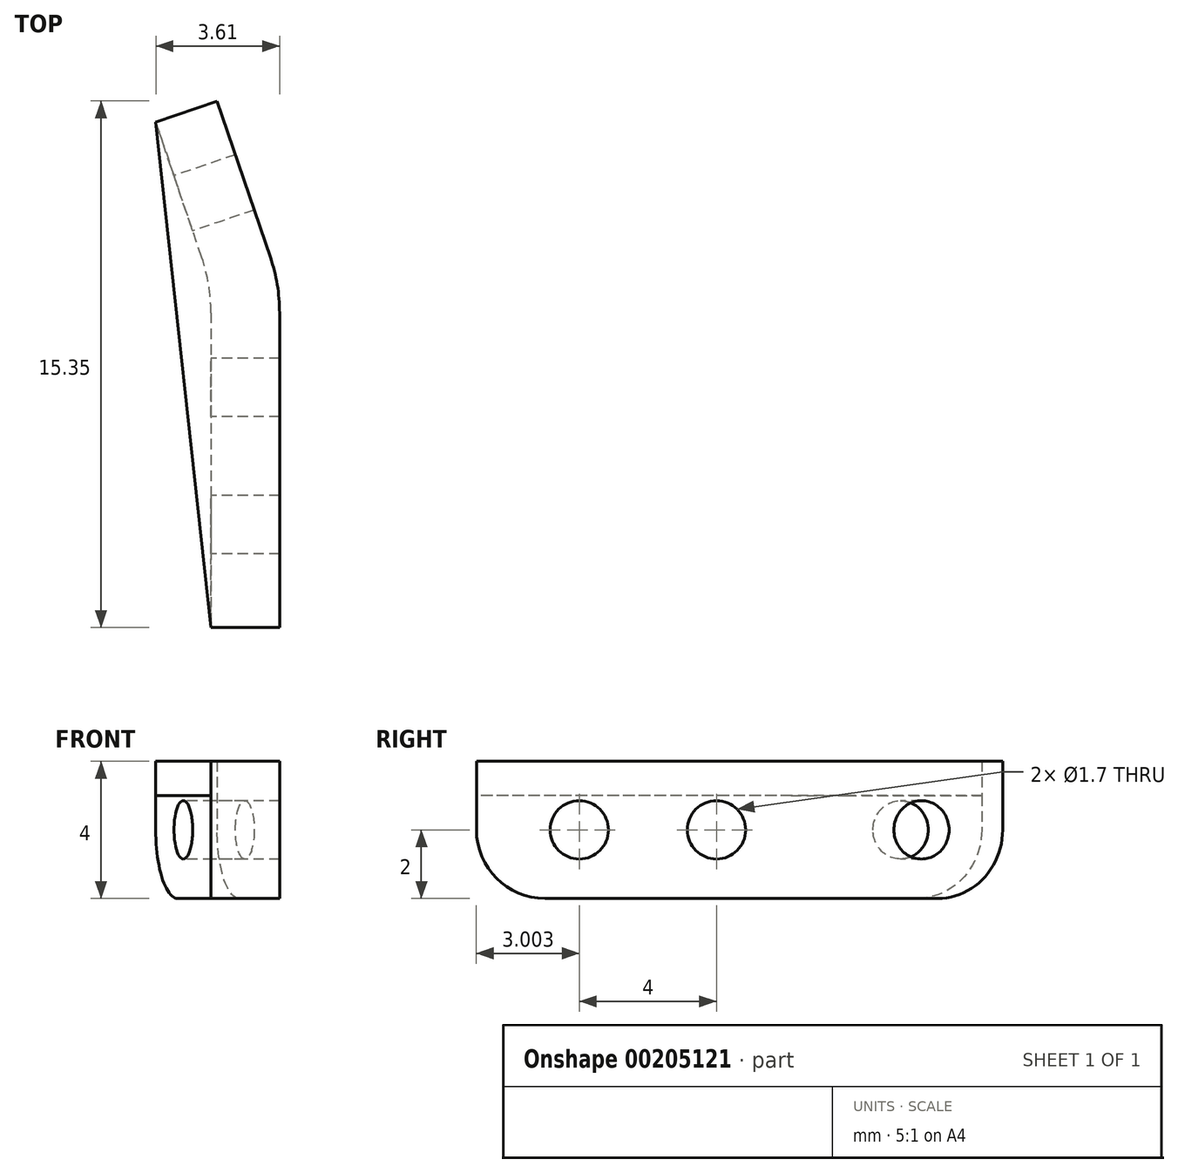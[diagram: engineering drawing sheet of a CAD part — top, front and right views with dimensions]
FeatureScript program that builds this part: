
annotation { "Feature Type Name" : "Feature", "Feature Type Description" : "" }
export const myFeature = defineFeature(function(context is Context, id is Id, definition is map)
    precondition{}
    {
        {
            var Q0;
            Q0=qCreatedBy(makeId("Top.planeOp"),FACE);
            var sketch = newSketch(context, id + "F0", { "sketchPlane" : qUnion([Q0])});
            skLineSegment(sketch, "E0.bottom", {"start": v(-12.73, -3.13) * mm, "end": v(-10.73, -3.13) * mm});
            skLineSegment(sketch, "E0.top", {"start": v(-12.73, -13.13) * mm, "end": v(-10.73, -13.13) * mm});
            skLineSegment(sketch, "E0.left", {"start": v(-12.73, -3.13) * mm, "end": v(-12.73, -13.13) * mm});
            skLineSegment(sketch, "E0.right", {"start": v(-10.73, -3.13) * mm, "end": v(-10.73, -13.13) * mm});
            skLineSegment(sketch, "E1", {"start": v(-12.73, -3.13) * mm, "end": v(-14.34, 1.6) * mm});
            skLineSegment(sketch, "E2", {"start": v(-14.34, 1.6) * mm, "end": v(-12.55, 2.22) * mm});
            skLineSegment(sketch, "E3", {"start": v(-12.55, 2.22) * mm, "end": v(-10.73, -3.13) * mm});
            skSolve(sketch);
        }
        {
            var Q0;
            Q0=makeQuery(id+"F0.imprint","IMPRINT",FACE,{"disambiguationData":[TD([[makeQuery(id+"F0.imprint","IMPRINT",EDGE,{"derivedFrom":sQuery(id+"F0.wireOp",EDGE,"E0.bottom")}),1.0]])]});
            var Q1;
            Q1=makeQuery(id+"F0.imprint","IMPRINT",FACE,{"disambiguationData":[TD([[makeQuery(id+"F0.imprint","IMPRINT",EDGE,{"derivedFrom":sQuery(id+"F0.wireOp",EDGE,"E0.bottom")}),-1.0]])]});
            extrude(context, id + "F1", {"entities" : qUnion([Q0, Q1]), "depth" : 4 * mm});
        }
        {
            var Q0;
            Q0=makeQuery(id+"F1.opExtrude","CAP_FACE",FACE,{"disambiguationData":[OSD([sQuery(id+"F0.wireOp",EDGE,"E0.top"),sQuery(id+"F0.wireOp",EDGE,"E0.left"),sQuery(id+"F0.wireOp",EDGE,"E0.right"),sQuery(id+"F0.wireOp",EDGE,"E1"),sQuery(id+"F0.wireOp",EDGE,"E2"),sQuery(id+"F0.wireOp",EDGE,"E3")])],"isStart":false});
            var sketch = newSketch(context, id + "F2", { "sketchPlane" : qUnion([Q0])});
            skLineSegment(sketch, "E4", {"start": v(-14.34, 1.6) * mm, "end": v(-12.73, -13.13) * mm});
            skLineSegment(sketch, "E5.0", {"start": v(-12.73, -3.13) * mm, "end": v(-14.34, 1.6) * mm});
            skLineSegment(sketch, "E6.0", {"start": v(-12.73, -3.13) * mm, "end": v(-12.73, -13.13) * mm});
            skSolve(sketch);
        }
        {
            var Q0;
            Q0 = qSketchRegion(id + "F2", true);
            extrude(context, id + "F3", {"entities" : qUnion([Q0]), "operationType" : NewBodyOperationType.ADD, "oppositeDirection" : true, "depth" : 1 * mm});
        }
        {
            var Q0;
            Q0=makeQuery(id+"F1.opExtrude","SWEPT_FACE",FACE,{"disambiguationData":[OSD([sQuery(id+"F0.wireOp",EDGE,"E1")])]});
            var sketch = newSketch(context, id + "F4", { "sketchPlane" : qUnion([Q0])});
            skCircle(sketch, "E7", {"center": v(-3.64, 2) * mm, "radius": 0.85 * mm});
            skPoint(sketch, "E7.centerSnap0", {"position": v(-3.64, 0) * mm});
            skSolve(sketch);
        }
        {
            var Q0;
            Q0=makeQuery(id+"F4.imprint","IMPRINT",FACE,{"disambiguationData":[TD([[makeQuery(id+"F4.imprint","IMPRINT",EDGE,{"derivedFrom":sQuery(id+"F4.wireOp",EDGE,"E7")}),1.0]])]});
            extrude(context, id + "F5", {"entities" : qUnion([Q0]), "operationType" : NewBodyOperationType.REMOVE, "oppositeDirection" : true, "depth" : 25 * mm});
        }
        {
            var Q0;
            Q0=makeQuery(id+"F1.opExtrude","SWEPT_FACE",FACE,{"disambiguationData":[OSD([sQuery(id+"F0.wireOp",EDGE,"E0.left")])]});
            var sketch = newSketch(context, id + "F6", { "sketchPlane" : qUnion([Q0])});
            skCircle(sketch, "E8", {"center": v(6.13, 2) * mm, "radius": 0.85 * mm});
            skEllipse(sketch, "E9.0", {"center": v(0.76, 2) * mm, "majorRadius": 0.85 * mm, "minorRadius": 0.8 * mm, "majorAxis": v(0, -1)});
            skCircle(sketch, "E10", {"center": v(10.13, 2) * mm, "radius": 0.85 * mm});
            skSolve(sketch);
        }
        {
            var Q0;
            Q0=makeQuery(id+"F6.imprint","IMPRINT",FACE,{"disambiguationData":[TD([[makeQuery(id+"F6.imprint","IMPRINT",EDGE,{"derivedFrom":sQuery(id+"F6.wireOp",EDGE,"E8")}),1.0]])]});
            var Q1;
            Q1=makeQuery(id+"F6.imprint","IMPRINT",FACE,{"disambiguationData":[TD([[makeQuery(id+"F6.imprint","IMPRINT",EDGE,{"derivedFrom":sQuery(id+"F6.wireOp",EDGE,"E10")}),1.0]])]});
            extrude(context, id + "F7", {"entities" : qUnion([Q0, Q1]), "operationType" : NewBodyOperationType.REMOVE, "oppositeDirection" : true, "depth" : 25 * mm});
        }
        {
            var Q0;
            Q0=makeQuery(id+"F1.opExtrude","SWEPT_EDGE",EDGE,{"disambiguationData":[OSD([sQuery(id+"F0.wireOp",EDGE,"E0.bottom"),sQuery(id+"F0.wireOp",EDGE,"E0.left"),sQuery(id+"F0.wireOp",EDGE,"E1")])]});
            fillet(context, id + "F8", {"entities" : qUnion([Q0]), "radius" : 5 * mm, "tangentPropagation" : true, "allowEdgeOverflow" : false});
        }
        {
            var Q0;
            Q0=makeQuery(id+"F1.opExtrude","SWEPT_EDGE",EDGE,{"disambiguationData":[OSD([sQuery(id+"F0.wireOp",EDGE,"E0.bottom"),sQuery(id+"F0.wireOp",EDGE,"E0.right"),sQuery(id+"F0.wireOp",EDGE,"E3")])]});
            fillet(context, id + "F9", {"entities" : qUnion([Q0]), "radius" : 5 * mm, "tangentPropagation" : true, "allowEdgeOverflow" : false});
        }
        {
            var Q0;
            Q0=makeQuery(id+"F1.opExtrude","CAP_EDGE",EDGE,{"disambiguationData":[OSD([sQuery(id+"F0.wireOp",EDGE,"E0.top")])],"isStart":true});
            var Q1;
            Q1=makeQuery(id+"F1.opExtrude","CAP_EDGE",EDGE,{"disambiguationData":[OSD([sQuery(id+"F0.wireOp",EDGE,"E2")])],"isStart":true});
            fillet(context, id + "F10", {"entities" : qUnion([Q0, Q1]), "radius" : 2 * mm, "tangentPropagation" : true, "allowEdgeOverflow" : false});
        }
    });
